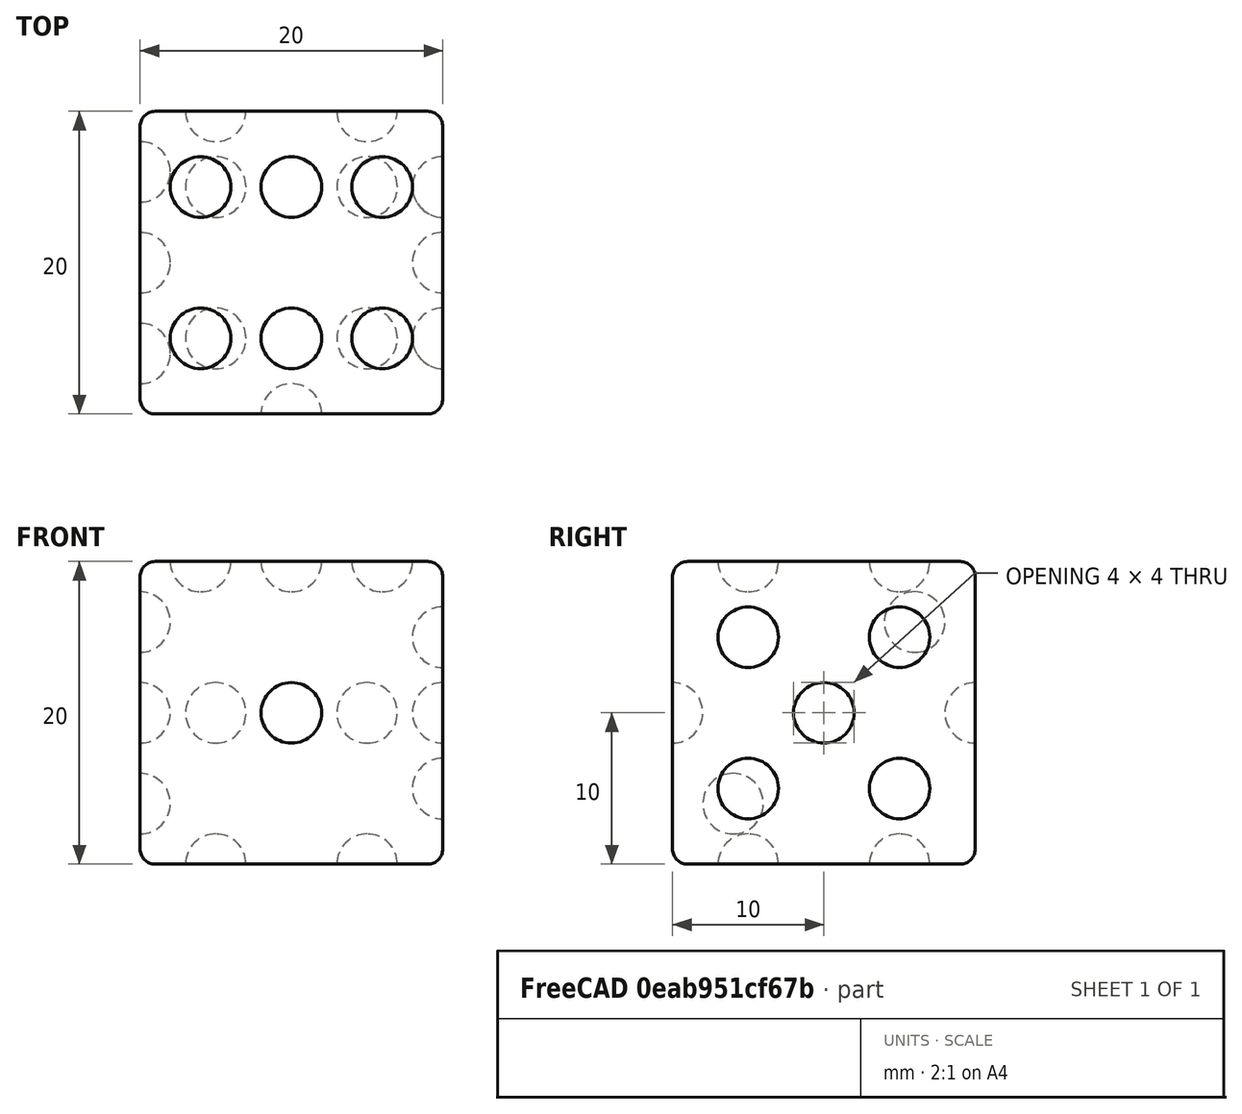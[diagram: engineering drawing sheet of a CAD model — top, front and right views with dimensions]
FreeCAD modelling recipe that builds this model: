
FCSTD DOCUMENT  (FreeCAD 0.16R6707 (Git))
Label: Dado
License: CreativeCommons Attribution-ShareAlike
LicenseURL: http://creativecommons.org/licenses/by-sa/4.0/
objects: Part::Sphere×8, Part::Cut×6, Part::FeaturePython×4, Part::MultiFuse×2, Part::Box×1, Part::Fillet×1
note: 22 computed .brp shape members not serialized (recipe doc carries the construction recipe); baked Part::Feature solids carry a one-line shape summary decoded from their .brp

FEATURE [Part::Box] Box  label="Base_Dado"
  Height = 20
  Length = 20
  Width = 20
FEATURE [Part::Fillet] Fillet  label="Dado_redondeado"
  Base = -> Box
  Edges = 12 edges r=1: [Edge1,Edge2,Edge3,Edge4,Edge5,Edge6,Edge7,Edge8,Edge9,Edge10,Edge11,Edge12]
FEATURE [Part::Sphere] Sphere
  Angle1 = -90
  Angle2 = 90
  Angle3 = 360
  Radius = 2
FEATURE [Part::FeaturePython] Array  label="Cara_6"  # Draft array (typed FeaturePython)
  Angle = 360
  ArrayType = 0
  Axis = (0,0,1)
  Base = -> Sphere
  Center = (0,0,0)
  Fuse = false
  IntervalAxis = (0,0,0)
  IntervalX = (6,0,0)
  IntervalY = (0,10,0)
  IntervalZ = (0,0,0)
  NumberPolar = 1
  NumberX = 3
  NumberY = 2
  NumberZ = 1
  Placement = pos=(4,5,20) rot=(0,0,1;0rad)
FEATURE [Part::Cut] Cut  label="Cara6"
  Base = -> Fillet
  Tool = -> Array
FEATURE [Part::Sphere] Sphere001
  Angle1 = -90
  Angle2 = 90
  Angle3 = 360
  Placement = pos=(10,0,10) rot=(0,0,1;0rad)
  Radius = 2
FEATURE [Part::Cut] Cut001  label="Cara1"
  Base = -> Cut
  Tool = -> Sphere001
FEATURE [Part::Sphere] Sphere002
  Angle1 = -90
  Angle2 = 90
  Angle3 = 360
  Placement = pos=(5,20,10) rot=(0,0,1;0rad)
  Radius = 2
FEATURE [Part::Sphere] Sphere003
  Angle1 = -90
  Angle2 = 90
  Angle3 = 360
  Placement = pos=(15,20,10) rot=(0,0,1;0rad)
  Radius = 2
FEATURE [Part::MultiFuse] Fusion  label="Numero2"
  Shapes = -> [Sphere003,Sphere002]
FEATURE [Part::Cut] Cut002  label="Cara2"
  Base = -> Cut001
  Tool = -> Fusion
FEATURE [Part::Sphere] Sphere004
  Angle1 = -90
  Angle2 = 90
  Angle3 = 360
  Radius = 2
FEATURE [Part::FeaturePython] Array001  label="Numero4"  # Draft array (typed FeaturePython)
  Angle = 360
  ArrayType = 0
  Axis = (0,0,1)
  Base = -> Sphere004
  Center = (0,0,0)
  Fuse = false
  IntervalAxis = (0,0,0)
  IntervalX = (10,0,0)
  IntervalY = (0,10,0)
  IntervalZ = (0,0,0)
  NumberPolar = 1
  NumberX = 2
  NumberY = 2
  NumberZ = 1
  Placement = pos=(5,5,0) rot=(0,0,1;0rad)
FEATURE [Part::Cut] Cut003  label="Cara4"
  Base = -> Cut002
  Tool = -> Array001
FEATURE [Part::Sphere] Sphere005
  Angle1 = -90
  Angle2 = 90
  Angle3 = 360
  Radius = 2
FEATURE [Part::FeaturePython] Array002  label="Numero3"  # Draft array (typed FeaturePython)
  Angle = 360
  ArrayType = 0
  Axis = (0,0,1)
  Base = -> Sphere005
  Center = (0,0,0)
  Fuse = false
  IntervalAxis = (0,0,0)
  IntervalX = (0,6,6)
  IntervalY = (0,1,0)
  IntervalZ = (0,0,0)
  NumberPolar = 1
  NumberX = 3
  NumberY = 1
  NumberZ = 1
  Placement = pos=(0,4,4) rot=(0,0,1;0rad)
FEATURE [Part::Cut] Cut004  label="Cara3"
  Base = -> Cut003
  Tool = -> Array002
FEATURE [Part::Sphere] Sphere006
  Angle1 = -90
  Angle2 = 90
  Angle3 = 360
  Radius = 2
FEATURE [Part::FeaturePython] Array003  # Draft array (typed FeaturePython)
  Angle = 360
  ArrayType = 0
  Axis = (0,0,1)
  Base = -> Sphere006
  Center = (0,0,0)
  Fuse = false
  IntervalAxis = (0,0,0)
  IntervalX = (10,0,0)
  IntervalY = (0,10,0)
  IntervalZ = (0,0,10)
  NumberPolar = 1
  NumberX = 1
  NumberY = 2
  NumberZ = 2
  Placement = pos=(20,5,5) rot=(0,0,1;0rad)
FEATURE [Part::Sphere] Sphere007
  Angle1 = -90
  Angle2 = 90
  Angle3 = 360
  Placement = pos=(20,10,10) rot=(0,0,1;0rad)
  Radius = 2
FEATURE [Part::MultiFuse] Fusion001  label="Cara5"
  Shapes = -> [Sphere007,Array003]
FEATURE [Part::Cut] Cut005  label="Dado"
  Base = -> Cut004
  Tool = -> Fusion001
